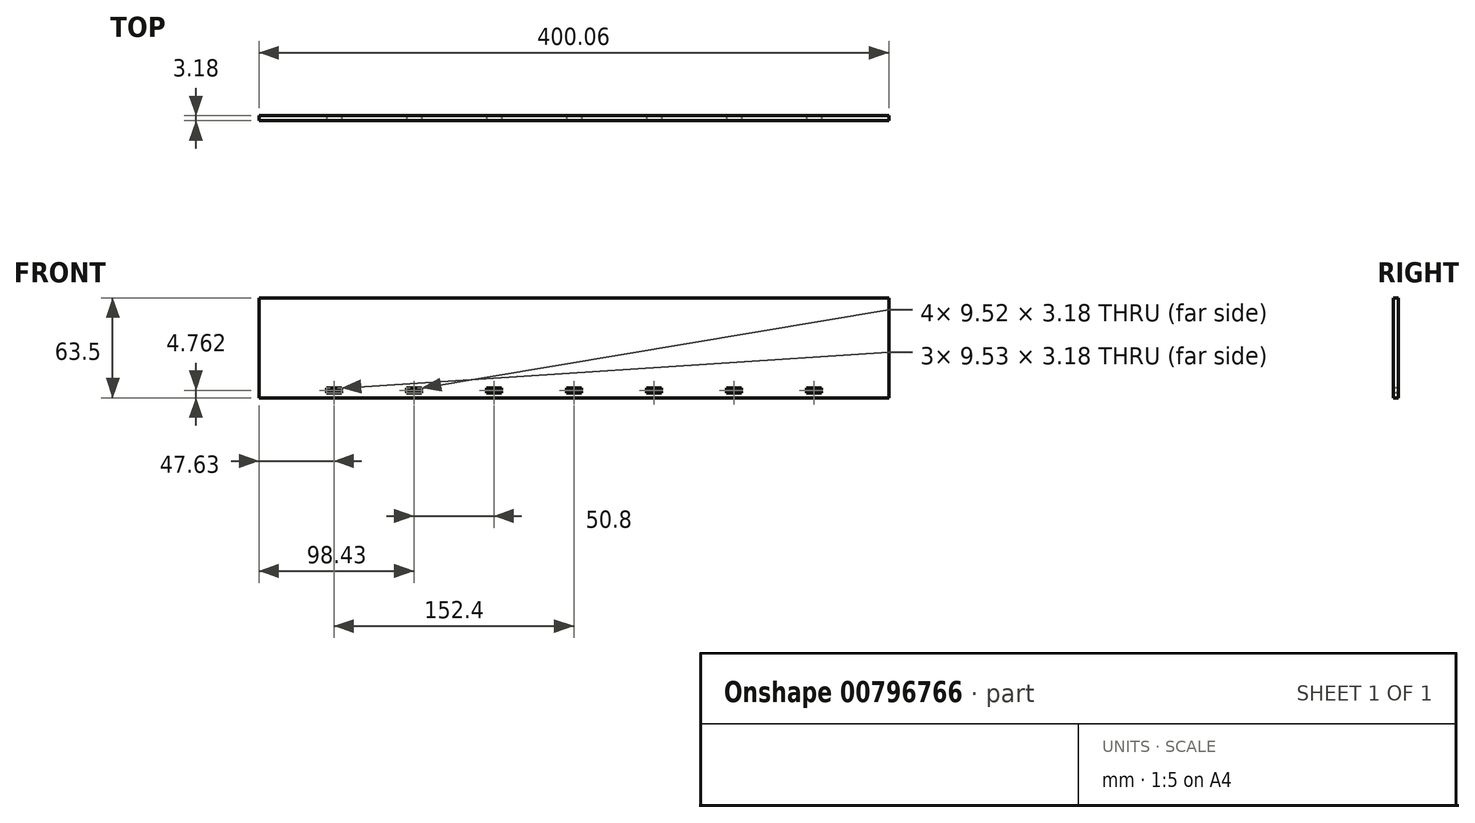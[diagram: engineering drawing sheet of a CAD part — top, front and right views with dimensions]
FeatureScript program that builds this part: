
annotation { "Feature Type Name" : "Feature", "Feature Type Description" : "" }
export const myFeature = defineFeature(function(context is Context, id is Id, definition is map)
    precondition{}
    {
        {
            var Q0;
            Q0=qCreatedBy(makeId("Front.planeOp"),FACE);
            var sketch = newSketch(context, id + "F0", { "sketchPlane" : qUnion([Q0])});
            skLineSegment(sketch, "E0.bottom", {"start": v(200.03, 31.75) * mm, "end": v(-200.02, 31.75) * mm});
            skLineSegment(sketch, "E0.top", {"start": v(200.02, -31.75) * mm, "end": v(-200.03, -31.75) * mm});
            skLineSegment(sketch, "E0.left", {"start": v(200.03, 31.75) * mm, "end": v(200.02, -31.75) * mm});
            skLineSegment(sketch, "E0.right", {"start": v(-200.02, 31.75) * mm, "end": v(-200.03, -31.75) * mm});
            skPoint(sketch, "E0.middle", {"position": v(0, 0) * mm});
            skSolve(sketch);
        }
        {
            var Q0;
            Q0=makeQuery(id+"F0.imprint","IMPRINT",FACE,{"disambiguationData":[TD([[makeQuery(id+"F0.imprint","IMPRINT",EDGE,{"derivedFrom":sQuery(id+"F0.wireOp",EDGE,"E0.bottom")}),1.0]])]});
            extrude(context, id + "F1", {"entities" : qUnion([Q0]), "depth" : 3.17 * mm, "offsetDistance" : 25.4 * mm});
        }
        {
            var Q0;
            Q0=makeQuery(id+"F1.opExtrude","CAP_FACE",FACE,{"disambiguationData":[OSD([sQuery(id+"F0.wireOp",EDGE,"E0.bottom"),sQuery(id+"F0.wireOp",EDGE,"E0.top"),sQuery(id+"F0.wireOp",EDGE,"E0.left"),sQuery(id+"F0.wireOp",EDGE,"E0.right")])],"isStart":false});
            var sketch = newSketch(context, id + "F2", { "sketchPlane" : qUnion([Q0])});
            skLineSegment(sketch, "E1", {"start": v(200.02, -28.58) * mm, "end": v(-200.03, -28.58) * mm, "construction": true});
            skLineSegment(sketch, "E2.bottom", {"start": v(157.16, -28.58) * mm, "end": v(147.64, -28.58) * mm});
            skLineSegment(sketch, "E2.top", {"start": v(157.16, -25.4) * mm, "end": v(147.64, -25.4) * mm});
            skLineSegment(sketch, "E2.left", {"start": v(157.16, -28.58) * mm, "end": v(157.16, -25.4) * mm});
            skLineSegment(sketch, "E2.right", {"start": v(147.64, -28.58) * mm, "end": v(147.64, -25.4) * mm});
            skLineSegment(sketch, "E3.bottom", {"start": v(106.36, -28.58) * mm, "end": v(96.84, -28.58) * mm});
            skLineSegment(sketch, "E3.top", {"start": v(106.36, -25.4) * mm, "end": v(96.84, -25.4) * mm});
            skLineSegment(sketch, "E3.left", {"start": v(106.36, -28.58) * mm, "end": v(106.36, -25.4) * mm});
            skLineSegment(sketch, "E3.right", {"start": v(96.84, -28.58) * mm, "end": v(96.84, -25.4) * mm});
            skLineSegment(sketch, "E4.bottom", {"start": v(55.56, -28.58) * mm, "end": v(46.04, -28.58) * mm});
            skLineSegment(sketch, "E4.top", {"start": v(55.56, -25.4) * mm, "end": v(46.04, -25.4) * mm});
            skLineSegment(sketch, "E4.left", {"start": v(55.56, -28.58) * mm, "end": v(55.56, -25.4) * mm});
            skLineSegment(sketch, "E4.right", {"start": v(46.04, -28.58) * mm, "end": v(46.04, -25.4) * mm});
            skPoint(sketch, "E5", {"position": v(152.4, -25.4) * mm});
            skPoint(sketch, "E6", {"position": v(101.6, -25.4) * mm});
            skPoint(sketch, "E7", {"position": v(50.8, -25.4) * mm});
            skLineSegment(sketch, "E8.MirrorCS", {"start": v(-106.36, -25.4) * mm, "end": v(-96.84, -25.4) * mm});
            skLineSegment(sketch, "E9.MirrorCS", {"start": v(-106.36, -28.58) * mm, "end": v(-106.36, -25.4) * mm});
            skLineSegment(sketch, "E10.MirrorCS", {"start": v(-96.84, -28.58) * mm, "end": v(-96.84, -25.4) * mm});
            skLineSegment(sketch, "E11.MirrorCS", {"start": v(-55.56, -28.58) * mm, "end": v(-46.04, -28.58) * mm});
            skLineSegment(sketch, "E12.MirrorCS", {"start": v(-55.56, -25.4) * mm, "end": v(-46.04, -25.4) * mm});
            skLineSegment(sketch, "E13.MirrorCS", {"start": v(-55.56, -28.58) * mm, "end": v(-55.56, -25.4) * mm});
            skLineSegment(sketch, "E14.MirrorCS", {"start": v(-46.04, -28.58) * mm, "end": v(-46.04, -25.4) * mm});
            skLineSegment(sketch, "E15.MirrorCS", {"start": v(-157.16, -28.58) * mm, "end": v(-147.64, -28.58) * mm});
            skLineSegment(sketch, "E16.MirrorCS", {"start": v(-157.16, -25.4) * mm, "end": v(-147.64, -25.4) * mm});
            skLineSegment(sketch, "E17.MirrorCS", {"start": v(-157.16, -28.58) * mm, "end": v(-157.16, -25.4) * mm});
            skPoint(sketch, "E18.MirrorP", {"position": v(-50.8, -25.4) * mm});
            skLineSegment(sketch, "E19.MirrorCS", {"start": v(-106.36, -28.58) * mm, "end": v(-96.84, -28.58) * mm});
            skPoint(sketch, "E20.MirrorP", {"position": v(-101.6, -25.4) * mm});
            skPoint(sketch, "E21.MirrorP", {"position": v(-152.4, -25.4) * mm});
            skLineSegment(sketch, "E22.MirrorCS", {"start": v(-147.64, -28.58) * mm, "end": v(-147.64, -25.4) * mm});
            skLineSegment(sketch, "E23.bottom", {"start": v(4.76, -28.58) * mm, "end": v(-4.76, -28.58) * mm});
            skLineSegment(sketch, "E23.top", {"start": v(4.76, -25.4) * mm, "end": v(-4.76, -25.4) * mm});
            skLineSegment(sketch, "E23.left", {"start": v(4.76, -28.58) * mm, "end": v(4.76, -25.4) * mm});
            skLineSegment(sketch, "E23.right", {"start": v(-4.76, -28.58) * mm, "end": v(-4.76, -25.4) * mm});
            skPoint(sketch, "E24", {"position": v(0, -25.4) * mm});
            skSolve(sketch);
        }
        {
            var Q0;
            Q0=qSketchRegion(id+"F2",true);
            extrude(context, id + "F3", {"entities" : qUnion([Q0]), "operationType" : NewBodyOperationType.REMOVE, "oppositeDirection" : true, "depth" : 25.4 * mm, "offsetDistance" : 25.4 * mm});
        }
    });
